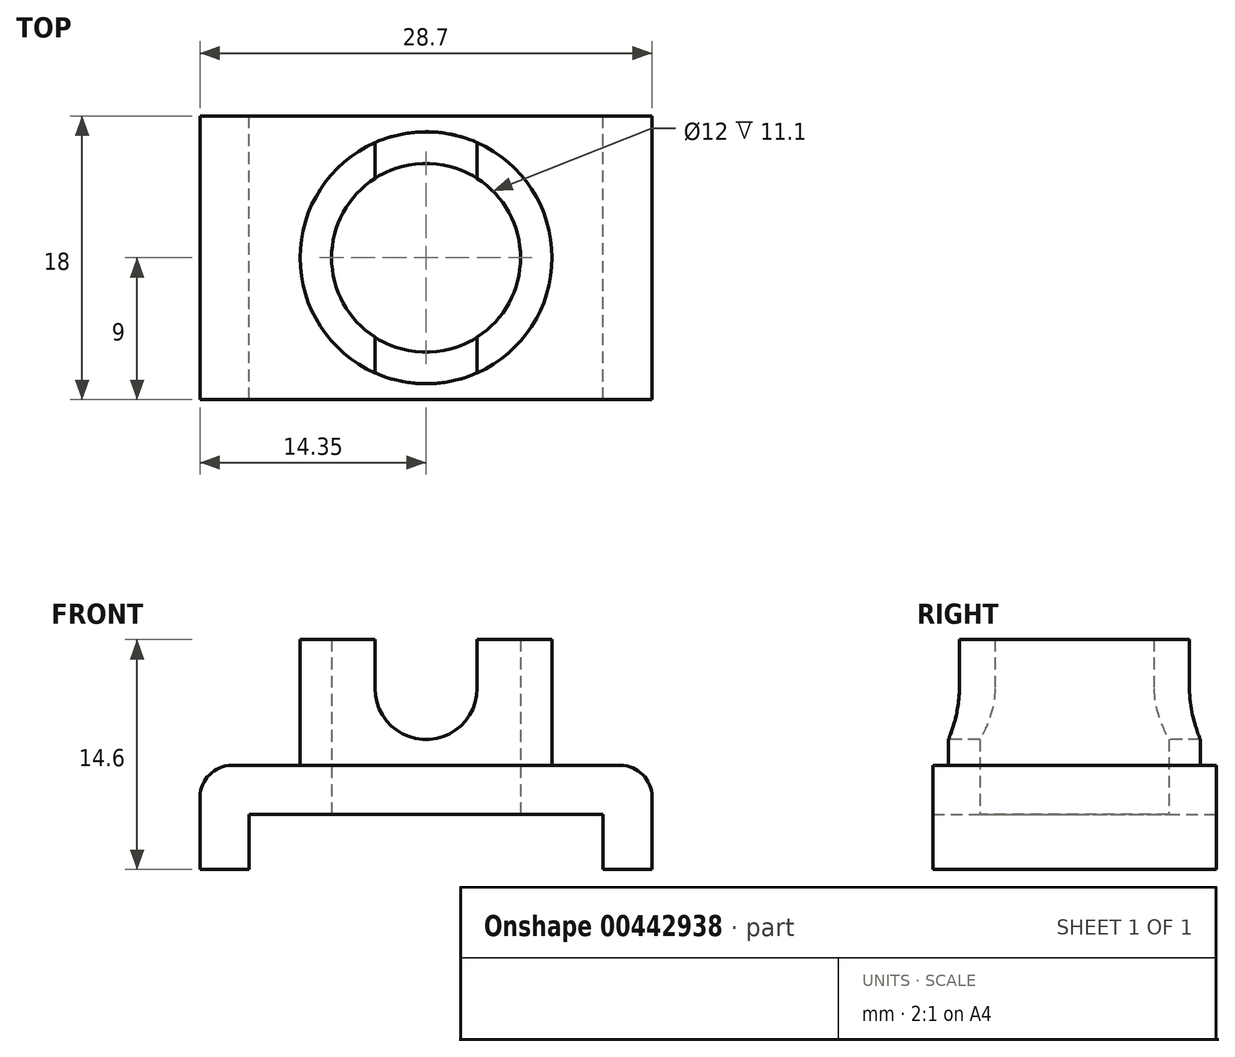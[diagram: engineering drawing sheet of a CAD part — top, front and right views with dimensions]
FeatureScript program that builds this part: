
annotation { "Feature Type Name" : "Feature", "Feature Type Description" : "" }
export const myFeature = defineFeature(function(context is Context, id is Id, definition is map)
    precondition{}
    {
        {
            var Q0;
            Q0=qCreatedBy(makeId("Front.planeOp"),FACE);
            var sketch = newSketch(context, id + "F0", { "sketchPlane" : qUnion([Q0])});
            skLineSegment(sketch, "E0.bottom", {"start": v(-14.35, 0) * mm, "end": v(14.35, 0) * mm});
            skLineSegment(sketch, "E0.top", {"start": v(-14.35, -6.6) * mm, "end": v(-11.25, -6.6) * mm});
            skLineSegment(sketch, "E0.left", {"start": v(-14.35, 0) * mm, "end": v(-14.35, -6.6) * mm});
            skLineSegment(sketch, "E0.right", {"start": v(14.35, 0) * mm, "end": v(14.35, -6.6) * mm});
            skLineSegment(sketch, "E1.top", {"start": v(-11.25, -3.1) * mm, "end": v(11.25, -3.1) * mm});
            skLineSegment(sketch, "E1.left", {"start": v(-11.25, -6.6) * mm, "end": v(-11.25, -3.1) * mm});
            skLineSegment(sketch, "E1.right", {"start": v(11.25, -6.6) * mm, "end": v(11.25, -3.1) * mm});
            skLineSegment(sketch, "E2.trimOffspring", {"start": v(11.25, -6.6) * mm, "end": v(14.35, -6.6) * mm});
            skLineSegment(sketch, "E3", {"start": v(0, 0) * mm, "end": v(0, 35.07) * mm, "construction": true});
            skLineSegment(sketch, "E4", {"start": v(-14.35, 0) * mm, "end": v(-11.25, -3.1) * mm, "construction": true});
            skSolve(sketch);
        }
        {
            var Q0;
            Q0 = qSketchRegion(id + "F0", true);
            extrude(context, id + "F1", {"entities" : qUnion([Q0]), "endBound" : BoundingType.SYMMETRIC, "depth" : 18 * mm, "offsetDistance" : 25 * mm});
        }
        {
            var Q0;
            Q0=makeQuery(id+"F1.opExtrude","SWEPT_EDGE",EDGE,{"disambiguationData":[OSD([sQuery(id+"F0.wireOp",EDGE,"E0.bottom"),sQuery(id+"F0.wireOp",EDGE,"E0.left")])]});
            var Q1;
            Q1=makeQuery(id+"F1.opExtrude","SWEPT_EDGE",EDGE,{"disambiguationData":[OSD([sQuery(id+"F0.wireOp",EDGE,"E0.bottom"),sQuery(id+"F0.wireOp",EDGE,"E0.right")])]});
            fillet(context, id + "F2", {"entities" : qUnion([Q0, Q1]), "radius" : 2 * mm, "tangentPropagation" : true, "allowEdgeOverflow" : false});
        }
        {
            var Q0;
            Q0=makeQuery(id+"F1.opExtrude","SWEPT_FACE",FACE,{"disambiguationData":[OSD([sQuery(id+"F0.wireOp",EDGE,"E0.bottom")])]});
            var sketch = newSketch(context, id + "F3", { "sketchPlane" : qUnion([Q0])});
            skCircle(sketch, "E5", {"center": v(0, 0) * mm, "radius": 7 * mm});
            skSolve(sketch);
        }
        {
            var Q0;
            Q0 = qSketchRegion(id + "F3", true);
            extrude(context, id + "F4", {"entities" : qUnion([Q0]), "operationType" : NewBodyOperationType.REMOVE, "endBound" : BoundingType.UP_TO_NEXT, "oppositeDirection" : true, "depth" : 25 * mm, "offsetDistance" : 25 * mm});
        }
        {
            var Q0;
            Q0=makeQuery(id+"F1.opExtrude","SWEPT_FACE",FACE,{"disambiguationData":[OSD([sQuery(id+"F0.wireOp",EDGE,"E0.bottom")])]});
            var sketch = newSketch(context, id + "F5", { "sketchPlane" : qUnion([Q0])});
            skCircle(sketch, "E6", {"center": v(0, 0) * mm, "radius": 8 * mm});
            skCircle(sketch, "E7.0", {"center": v(0, 0) * mm, "radius": 5 * mm});
            skSolve(sketch);
        }
        {
            var Q0;
            Q0 = qSketchRegion(id + "F5", true);
            extrude(context, id + "F6", {"entities" : qUnion([Q0]), "depth" : 8 * mm, "offsetDistance" : 25 * mm});
        }
        {
            var Q0;
            Q0=makeQuery(id+"F6.opExtrude","CAP_FACE",FACE,{"disambiguationData":[OSD([sQuery(id+"F5.wireOp",EDGE,"E6"),sQuery(id+"F5.wireOp",EDGE,"E7.0")])],"isStart":true});
            var sketch = newSketch(context, id + "F7", { "sketchPlane" : qUnion([Q0])});
            skCircle(sketch, "E8.0", {"center": v(0, 0) * mm, "radius": 5 * mm});
            skCircle(sketch, "E9.0", {"center": v(0, 0) * mm, "radius": 7 * mm});
            skSolve(sketch);
        }
        {
            var Q0;
            Q0 = qSketchRegion(id + "F7", true);
            var Q1;
            Q1=makeQuery(id+"F1.opExtrude","SWEPT_FACE",FACE,{"disambiguationData":[OSD([sQuery(id+"F0.wireOp",EDGE,"E1.top")])]});
            extrude(context, id + "F8", {"entities" : qUnion([Q0]), "operationType" : NewBodyOperationType.ADD, "endBound" : BoundingType.UP_TO_SURFACE, "depth" : 25 * mm, "endBoundEntityFace" : qUnion([Q1]), "offsetDistance" : 25 * mm});
        }
        {
            var Q0;
            Q0=qCreatedBy(makeId("Front.planeOp"),FACE);
            var sketch = newSketch(context, id + "F9", { "sketchPlane" : qUnion([Q0])});
            skArc(sketch, "E10", {"start": v(-3.25, 4.9) * mm, "mid": v(0, 1.65) * mm, "end": v(3.25, 4.9) * mm});
            skLineSegment(sketch, "E11.top", {"start": v(-3.25, 8) * mm, "end": v(3.25, 8) * mm});
            skLineSegment(sketch, "E11.left", {"start": v(-3.25, 4.9) * mm, "end": v(-3.25, 8) * mm});
            skLineSegment(sketch, "E11.right", {"start": v(3.25, 4.9) * mm, "end": v(3.25, 8) * mm});
            skSolve(sketch);
        }
        {
            var Q0;
            Q0 = qSketchRegion(id + "F9", true);
            extrude(context, id + "F10", {"entities" : qUnion([Q0]), "operationType" : NewBodyOperationType.REMOVE, "endBound" : BoundingType.SYMMETRIC, "oppositeDirection" : true, "depth" : 25 * mm});
        }
        {
            var Q0;
            Q0=makeQuery(id+"F8.opExtrude","CAP_FACE",FACE,{"disambiguationData":[OSD([sQuery(id+"F7.wireOp",EDGE,"E8.0"),sQuery(id+"F7.wireOp",EDGE,"E9.0")])],"isStart":false});
            var sketch = newSketch(context, id + "F11", { "sketchPlane" : qUnion([Q0])});
            skCircle(sketch, "E12", {"center": v(0, 0) * mm, "radius": 6 * mm});
            skSolve(sketch);
        }
        {
            var Q0;
            Q0 = qSketchRegion(id + "F11", true);
            extrude(context, id + "F12", {"entities" : qUnion([Q0]), "operationType" : NewBodyOperationType.REMOVE, "endBound" : BoundingType.THROUGH_ALL, "oppositeDirection" : true, "depth" : 25 * mm, "offsetDistance" : 25 * mm});
        }
    });
